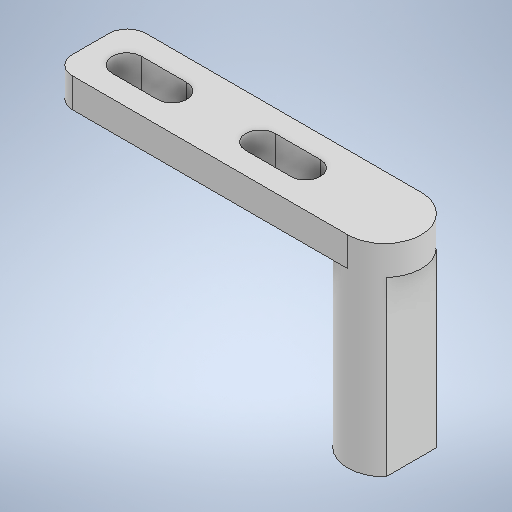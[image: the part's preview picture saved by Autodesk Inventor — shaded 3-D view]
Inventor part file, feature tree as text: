
AUTODESK INVENTOR PART (.ipt)
format: ipt  version: 2025 (Build 290162000, 162)  size: 280,064 bytes
history: native  units: in
note: dims shown in document units (in); Inventor stores cm internally (conversion verified against a paired STEP export)
features: extrude x3, sketch x3, projected_geometry x2
ambient origin geometry x8: Origin, YZ Plane, XZ Plane, XY Plane, X Axis, Y Axis, Z Axis, Center Point
bodies: Solid1 (feature_tree)
feature tree (8):
  extrude  "Extrusion1"  Depth=0.2756in
  extrude  "Extrusion2"  Depth=0.0591in
  extrude  "Extrusion4"  Depth=0.0984in TaperAngle=0.0deg
  sketch  "Sketch1"  dims[d0=0.2756in d1=0.2205in]
  sketch  "Sketch2"  dims[d2=0.1181in d3=0.0591in]
  projected_geometry  "Projected Loop1"
  sketch  "Sketch4"  dims[d4=0.8268in d5=0.0in d6=0.0984in d7=0.0in d12=0.1374in d13=0.4724in d28=1.5748in d29=0.0984in d30=0.1575in d31=0.315in d32=0.1575in d33=1.0451in d34=0.1575in d35=0.0in]
  projected_geometry  "Projected Loop3"
